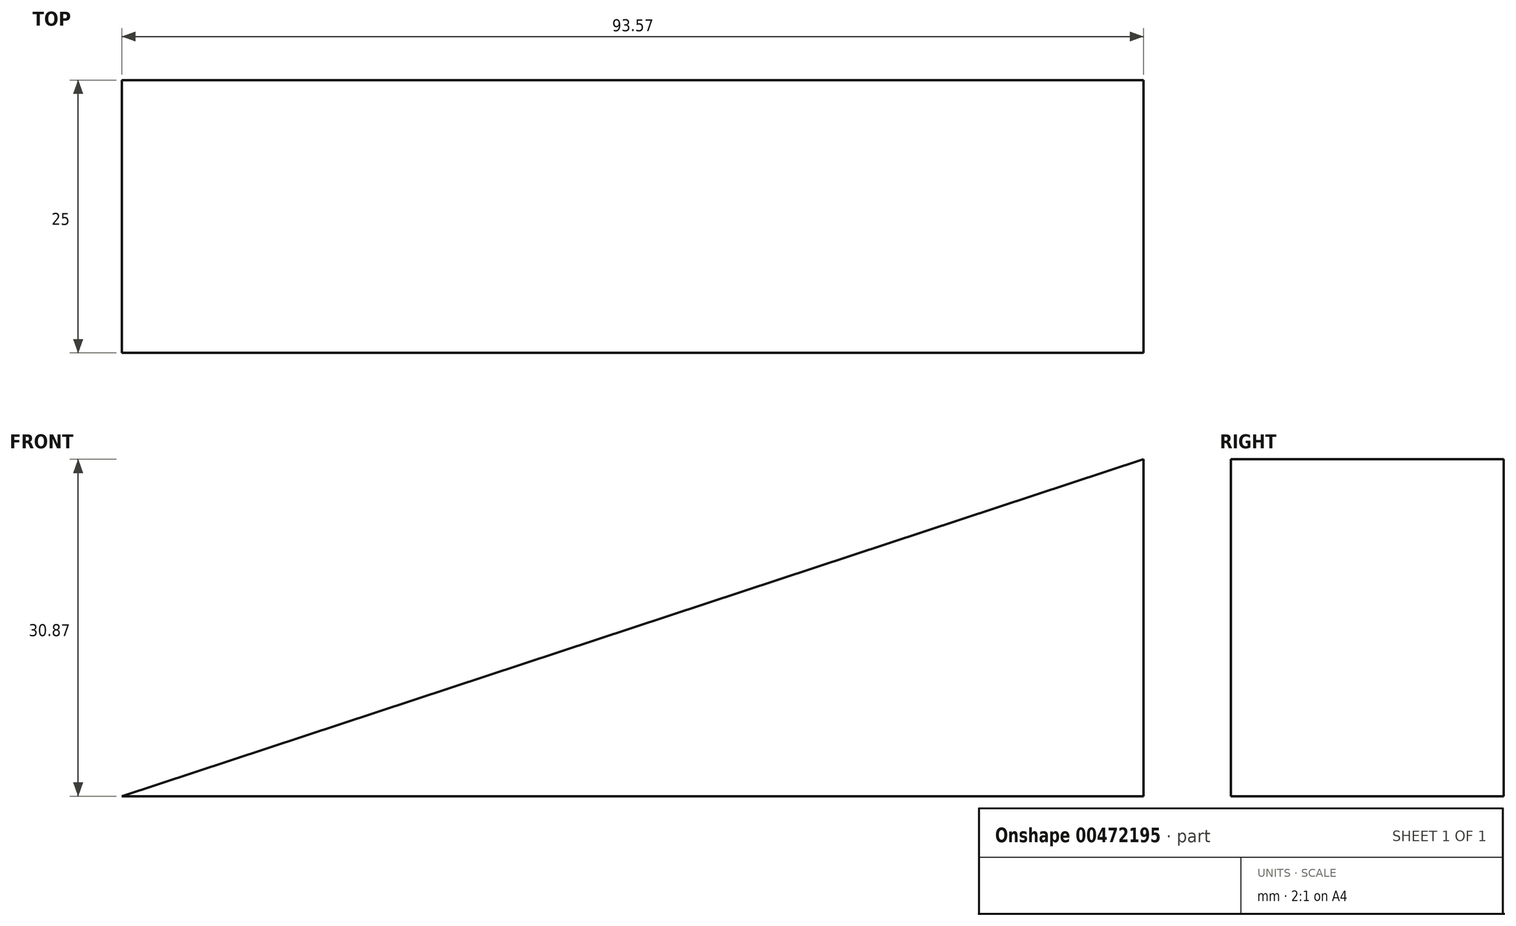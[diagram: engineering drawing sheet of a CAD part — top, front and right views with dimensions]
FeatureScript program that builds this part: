
annotation { "Feature Type Name" : "Feature", "Feature Type Description" : "" }
export const myFeature = defineFeature(function(context is Context, id is Id, definition is map)
    precondition{}
    {
        {
            var Q0;
            Q0=qCreatedBy(makeId("Front.planeOp"),FACE);
            var sketch = newSketch(context, id + "F0", { "sketchPlane" : qUnion([Q0])});
            skLineSegment(sketch, "E0", {"start": v(-53.33, 0) * mm, "end": v(40.24, 0) * mm});
            skLineSegment(sketch, "E1", {"start": v(40.24, 0) * mm, "end": v(40.24, 30.87) * mm});
            skLineSegment(sketch, "E2", {"start": v(40.24, 30.87) * mm, "end": v(-53.33, 0) * mm});
            skLineSegment(sketch, "E3", {"start": v(0, 0) * mm, "end": v(0, 17.6) * mm});
            skLineSegment(sketch, "E4", {"start": v(4.64, 0) * mm, "end": v(4.64, 19.12) * mm});
            skSolve(sketch);
        }
        {
            var Q0;
            {var subQ3=sQuery(id+"F0.wireOp",EDGE,"E3");Q0=makeQuery(id+"F0.imprint","IMPRINT",FACE,{"disambiguationData":[TD([[makeQuery(id+"F0.imprint","IMPRINT",EDGE,{"derivedFrom":subQ3}),1.0]])]});}
            var Q1;
            {var subQ0=sQuery(id+"F0.wireOp",EDGE,"E1");Q1=makeQuery(id+"F0.imprint","IMPRINT",FACE,{"disambiguationData":[TD([[makeQuery(id+"F0.imprint","IMPRINT",EDGE,{"derivedFrom":subQ0}),1.0]])]});}
            var Q2;
            Q2 = qSketchRegion(id + "F0", true);
            extrude(context, id + "F1", {"entities" : qUnion([Q0, Q1, Q2]), "depth" : 25 * mm});
        }
    });
